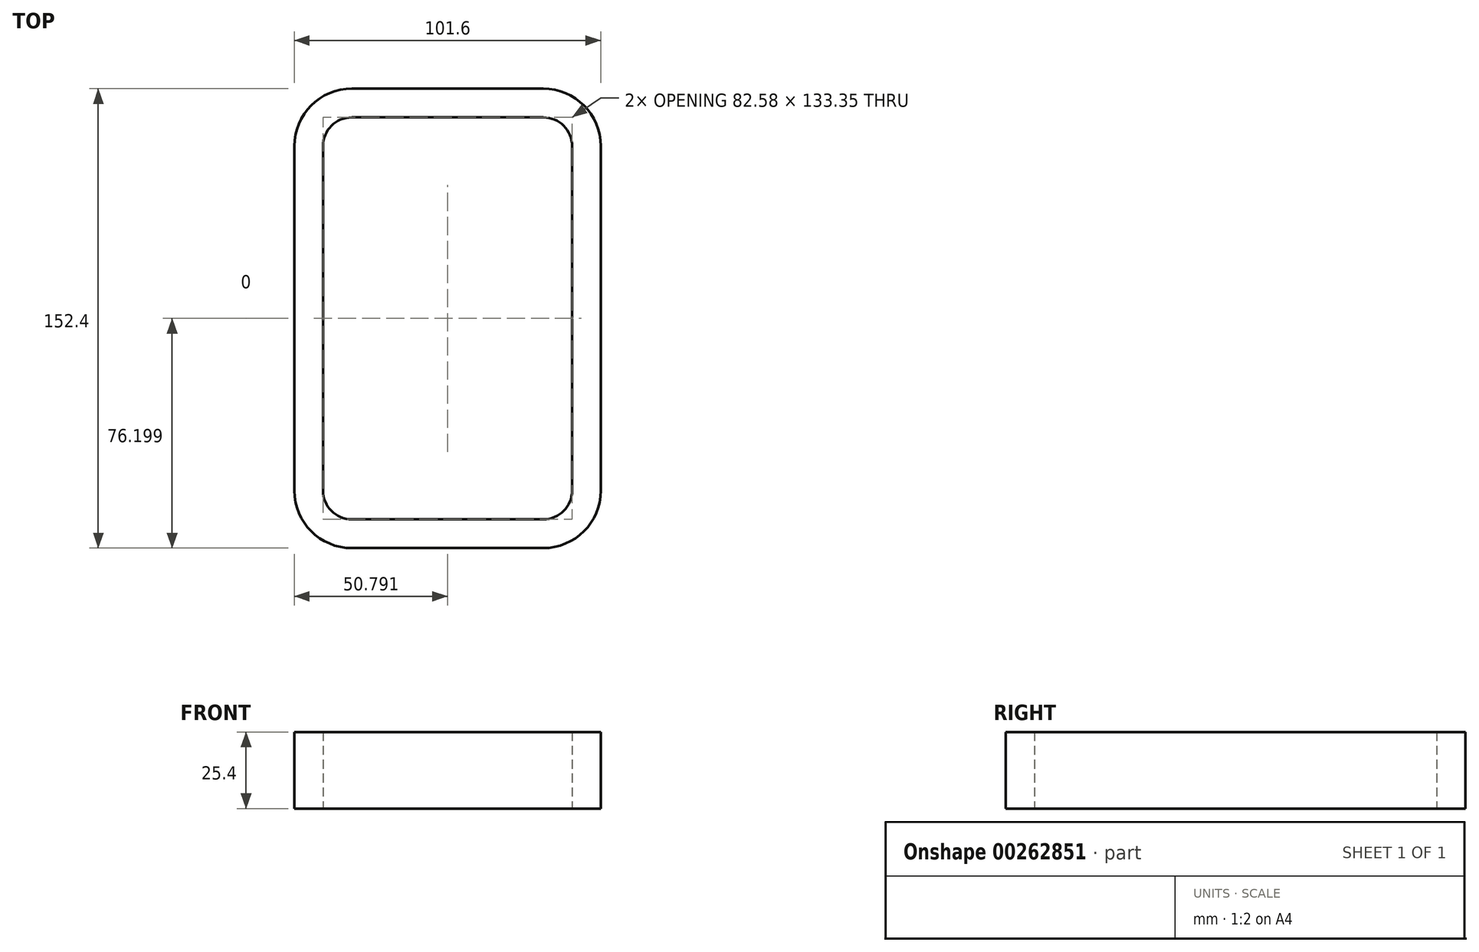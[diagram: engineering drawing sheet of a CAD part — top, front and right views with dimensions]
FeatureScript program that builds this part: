
annotation { "Feature Type Name" : "Feature", "Feature Type Description" : "" }
export const myFeature = defineFeature(function(context is Context, id is Id, definition is map)
    precondition{}
    {
        {
            var Q0;
            Q0=qCreatedBy(makeId("Top.planeOp"),FACE);
            var sketch = newSketch(context, id + "F0", { "sketchPlane" : qUnion([Q0])});
            skLineSegment(sketch, "E0.bottom", {"start": v(-30.24, 73.73) * mm, "end": v(33.26, 73.73) * mm});
            skLineSegment(sketch, "E0.top", {"start": v(-30.24, -78.67) * mm, "end": v(33.26, -78.67) * mm});
            skLineSegment(sketch, "E1.bottom", {"start": v(-30.26, 64.2) * mm, "end": v(33.26, 64.2) * mm});
            skLineSegment(sketch, "E1.top", {"start": v(-30.26, -69.15) * mm, "end": v(33.26, -69.15) * mm});
            skPoint(sketch, "E2.visualSharp", {"position": v(-30.2, 64.2) * mm});
            skArc(sketch, "E2.filletArc", {"start": v(-30.26, 64.2) * mm, "mid": v(-37, 61.41) * mm, "end": v(-39.79, 54.68) * mm});
            skPoint(sketch, "E3.visualSharp", {"position": v(-30.2, -69.15) * mm});
            skArc(sketch, "E3.filletArc", {"start": v(-39.79, -59.62) * mm, "mid": v(-37, -66.36) * mm, "end": v(-30.26, -69.15) * mm});
            skPoint(sketch, "E4.visualSharp", {"position": v(52.36, -69.15) * mm});
            skArc(sketch, "E4.filletArc", {"start": v(33.26, -69.15) * mm, "mid": v(40, -66.36) * mm, "end": v(42.79, -59.62) * mm});
            skPoint(sketch, "E5.visualSharp", {"position": v(52.36, 64.2) * mm});
            skArc(sketch, "E5.filletArc", {"start": v(42.79, 54.68) * mm, "mid": v(40, 61.41) * mm, "end": v(33.26, 64.2) * mm});
            skPoint(sketch, "E6.visualSharp", {"position": v(-39.72, 73.73) * mm});
            skArc(sketch, "E6.filletArc", {"start": v(-30.24, 73.73) * mm, "mid": v(-43.7, 68.15) * mm, "end": v(-49.29, 54.68) * mm});
            skPoint(sketch, "E7.visualSharp", {"position": v(-39.72, -78.67) * mm});
            skArc(sketch, "E7.filletArc", {"start": v(-49.29, -59.62) * mm, "mid": v(-43.7, -73.1) * mm, "end": v(-30.24, -78.67) * mm});
            skPoint(sketch, "E8.visualSharp", {"position": v(61.88, -78.67) * mm});
            skArc(sketch, "E8.filletArc", {"start": v(33.26, -78.67) * mm, "mid": v(46.73, -73.1) * mm, "end": v(52.31, -59.62) * mm});
            skPoint(sketch, "E9.visualSharp", {"position": v(61.88, 73.73) * mm});
            skArc(sketch, "E9.filletArc", {"start": v(52.31, 54.68) * mm, "mid": v(46.73, 68.15) * mm, "end": v(33.26, 73.73) * mm});
            skLineSegment(sketch, "E10", {"start": v(-49.29, 54.68) * mm, "end": v(-49.29, -59.62) * mm});
            skLineSegment(sketch, "E11", {"start": v(-39.79, 54.68) * mm, "end": v(-39.79, -59.62) * mm});
            skLineSegment(sketch, "E12", {"start": v(42.79, 54.68) * mm, "end": v(42.79, -59.62) * mm});
            skLineSegment(sketch, "E13", {"start": v(52.31, 54.68) * mm, "end": v(52.31, -59.62) * mm});
            skSolve(sketch);
        }
        {
            var Q0;
            Q0 = qSketchRegion(id + "F0", true);
            extrude(context, id + "F1", {"entities" : qUnion([Q0]), "depth" : 25.4 * mm});
        }
        {
            var Q0;
            Q0=makeQuery(id+"F1.opExtrude","SWEPT_BODY",BODY,{"disambiguationData":[OSD([sQuery(id+"F0.wireOp",EDGE,"E0.bottom"),sQuery(id+"F0.wireOp",EDGE,"E0.top"),sQuery(id+"F0.wireOp",EDGE,"E1.bottom"),sQuery(id+"F0.wireOp",EDGE,"E1.top"),sQuery(id+"F0.wireOp",EDGE,"E2.filletArc"),sQuery(id+"F0.wireOp",EDGE,"E3.filletArc"),sQuery(id+"F0.wireOp",EDGE,"E4.filletArc"),sQuery(id+"F0.wireOp",EDGE,"E5.filletArc"),sQuery(id+"F0.wireOp",EDGE,"E6.filletArc"),sQuery(id+"F0.wireOp",EDGE,"E7.filletArc"),sQuery(id+"F0.wireOp",EDGE,"E8.filletArc"),sQuery(id+"F0.wireOp",EDGE,"E9.filletArc"),sQuery(id+"F0.wireOp",EDGE,"E10"),sQuery(id+"F0.wireOp",EDGE,"E11"),sQuery(id+"F0.wireOp",EDGE,"E12"),sQuery(id+"F0.wireOp",EDGE,"E13")])]});
            transform(context, id + "F2", {"entities" : qUnion([Q0]), "transformType" : TransformType.TRANSLATION_3D, "dx" : 0 * mm, "dy" : 0 * mm, "dz" : 0 * mm, "makeCopy" : true});
        }
    });
